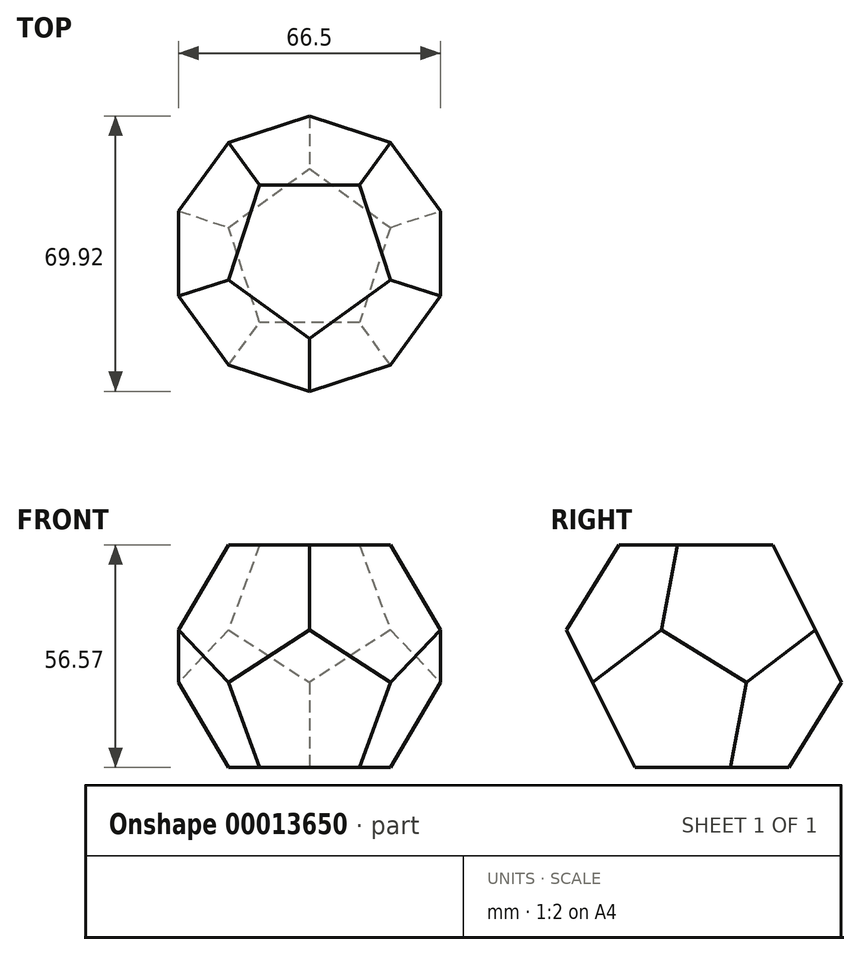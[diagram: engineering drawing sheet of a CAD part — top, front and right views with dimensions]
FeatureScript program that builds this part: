
annotation { "Feature Type Name" : "Feature", "Feature Type Description" : "" }
export const myFeature = defineFeature(function(context is Context, id is Id, definition is map)
    precondition{}
    {
        {
            var Q0;
            Q0=qCreatedBy(makeId("Top.planeOp"),FACE);
            var sketch = newSketch(context, id + "F0", { "sketchPlane" : qUnion([Q0])});
            skCircle(sketch, "E0.cCircle", {"center": v(0, 0) * mm, "radius": 17.48 * mm, "construction": true});
            skLineSegment(sketch, "E0.0", {"start": v(12.7, -17.48) * mm, "end": v(-12.7, -17.48) * mm});
            skLineSegment(sketch, "E0.1", {"start": v(-12.7, -17.48) * mm, "end": v(-20.55, 6.68) * mm});
            skLineSegment(sketch, "E0.2", {"start": v(-20.55, 6.68) * mm, "end": v(0, 21.6) * mm});
            skLineSegment(sketch, "E0.3", {"start": v(0, 21.6) * mm, "end": v(20.55, 6.68) * mm});
            skLineSegment(sketch, "E0.4", {"start": v(20.55, 6.68) * mm, "end": v(12.7, -17.48) * mm});
            skPoint(sketch, "E0.0.midPoint", {"position": v(0, -17.48) * mm});
            skSolve(sketch);
        }
        {
            var Q0;
            Q0=makeQuery(id+"F0.imprint","IMPRINT",FACE,{"disambiguationData":[TD([[makeQuery(id+"F0.imprint","IMPRINT",EDGE,{"derivedFrom":sQuery(id+"F0.wireOp",EDGE,"E0.0")}),-1.0]])]});
            extrude(context, id + "F1", {"entities" : qUnion([Q0]), "depth" : 25374.6 * mm, "hasDraft" : true, "draftAngle" : atan(2) / 2, "draftPullDirection" : true});
        }
        {
            var Q0;
            Q0=makeQuery(id+"F1.opExtrude","SWEPT_BODY",BODY,{"disambiguationData":[OSD([sQuery(id+"F0.wireOp",EDGE,"E0.0"),sQuery(id+"F0.wireOp",EDGE,"E0.1"),sQuery(id+"F0.wireOp",EDGE,"E0.2"),sQuery(id+"F0.wireOp",EDGE,"E0.3"),sQuery(id+"F0.wireOp",EDGE,"E0.4")])]});
            var Q1;
            Q1=makeQuery(id+"F1.opExtrude","SWEPT_EDGE",EDGE,{"disambiguationData":[OSD([sQuery(id+"F0.wireOp",EDGE,"E0.0"),sQuery(id+"F0.wireOp",EDGE,"E0.4")])]});
            circularPattern(context, id + "F2", {"operationType" : NewBodyOperationType.ADD, "entities" : qUnion([Q0]), "axis" : qUnion([Q1]), "angle" : 360 * degree, "instanceCount" : round(3), "equalSpace" : true});
        }
        {
            var Q0;
            Q0=makeQuery(id+"F1.opExtrude","SWEPT_BODY",BODY,{"disambiguationData":[OSD([sQuery(id+"F0.wireOp",EDGE,"E0.0"),sQuery(id+"F0.wireOp",EDGE,"E0.1"),sQuery(id+"F0.wireOp",EDGE,"E0.2"),sQuery(id+"F0.wireOp",EDGE,"E0.3"),sQuery(id+"F0.wireOp",EDGE,"E0.4")])]});
            var Q1;
            Q1=makeQuery(id+"F1.opExtrude","SWEPT_EDGE",EDGE,{"disambiguationData":[OSD([sQuery(id+"F0.wireOp",EDGE,"E0.1"),sQuery(id+"F0.wireOp",EDGE,"E0.2")])]});
            circularPattern(context, id + "F3", {"operationType" : NewBodyOperationType.ADD, "entities" : qUnion([Q0]), "axis" : qUnion([Q1]), "angle" : 360 * degree, "instanceCount" : round(3), "equalSpace" : true});
        }
        {
            var Q0;
            Q0=makeQuery(id+"F1.opExtrude","SWEPT_BODY",BODY,{"disambiguationData":[OSD([sQuery(id+"F0.wireOp",EDGE,"E0.0"),sQuery(id+"F0.wireOp",EDGE,"E0.1"),sQuery(id+"F0.wireOp",EDGE,"E0.2"),sQuery(id+"F0.wireOp",EDGE,"E0.3"),sQuery(id+"F0.wireOp",EDGE,"E0.4")])]});
            var Q1;
            Q1=makeQuery(id+"F2.opPattern","COPY",FACE,{"derivedFrom":makeQuery(id+"F1.opExtrude","SWEPT_FACE",FACE,{"disambiguationData":[OSD([sQuery(id+"F0.wireOp",EDGE,"E0.1")])]}),"instanceName":"2"});
            mirror(context, id + "F4", {"operationType" : NewBodyOperationType.ADD, "entities" : qUnion([Q0]), "mirrorPlane" : qUnion([Q1])});
        }
    });
